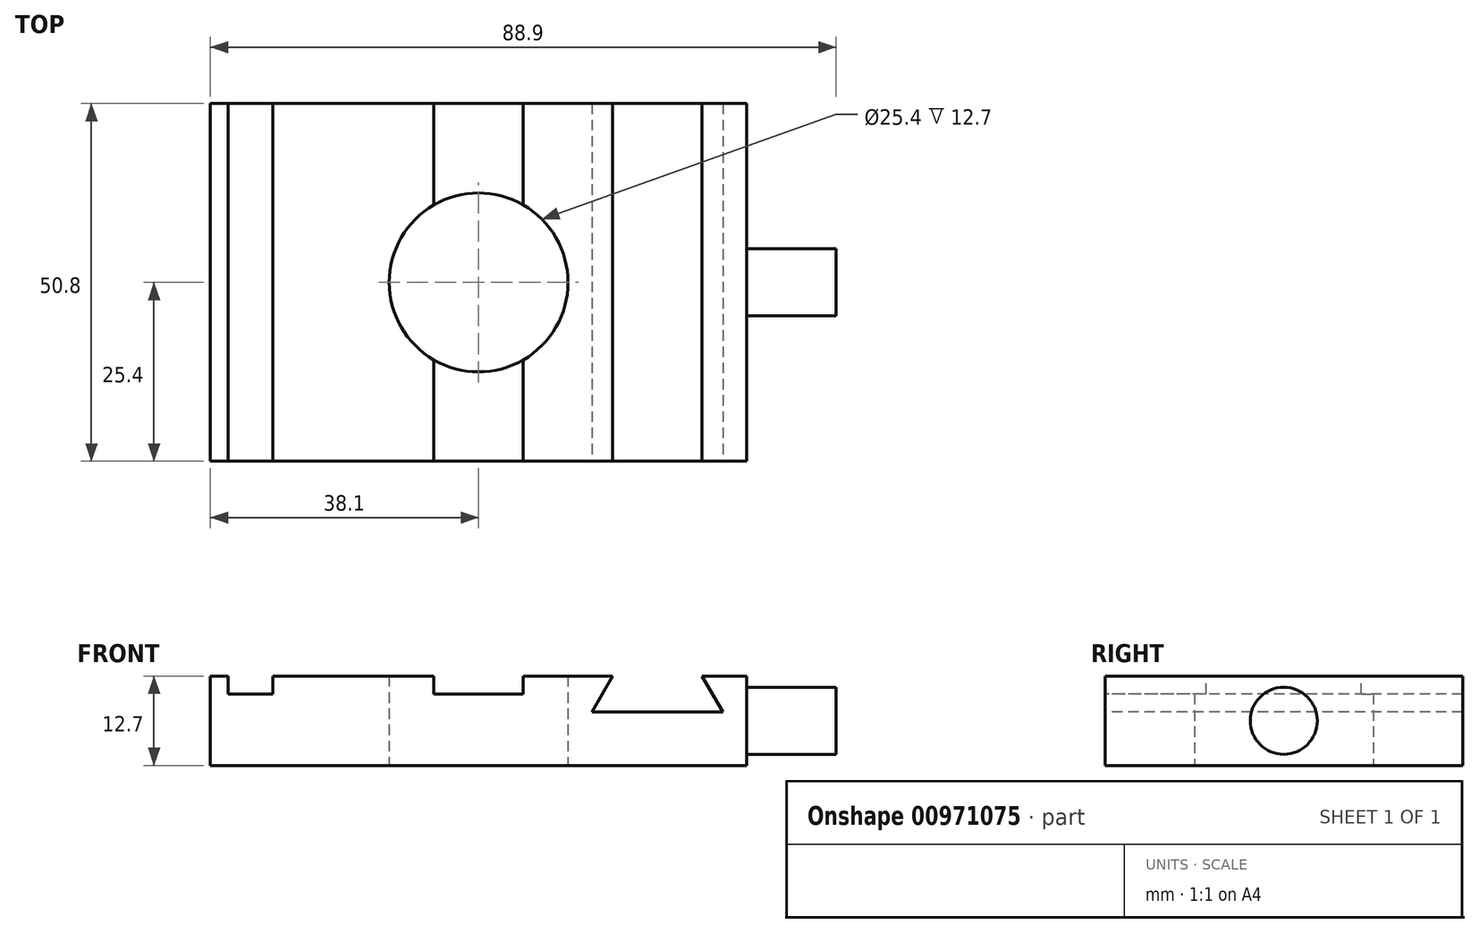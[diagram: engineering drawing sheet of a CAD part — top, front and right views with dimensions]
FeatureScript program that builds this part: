
annotation { "Feature Type Name" : "Feature", "Feature Type Description" : "" }
export const myFeature = defineFeature(function(context is Context, id is Id, definition is map)
    precondition{}
    {
        {
            var Q0;
            Q0=qCreatedBy(makeId("Top.planeOp"),FACE);
            var sketch = newSketch(context, id + "F0", { "sketchPlane" : qUnion([Q0])});
            skLineSegment(sketch, "E0.bottom", {"start": v(-38.1, -25.4) * mm, "end": v(38.1, -25.4) * mm});
            skLineSegment(sketch, "E0.top", {"start": v(-38.1, 25.4) * mm, "end": v(38.1, 25.4) * mm});
            skLineSegment(sketch, "E0.left", {"start": v(-38.1, -25.4) * mm, "end": v(-38.1, 25.4) * mm});
            skLineSegment(sketch, "E0.right", {"start": v(38.1, -25.4) * mm, "end": v(38.1, 25.4) * mm});
            skPoint(sketch, "E0.middle", {"position": v(0, 0) * mm});
            skCircle(sketch, "E1", {"center": v(0, 0) * mm, "radius": 12.7 * mm});
            skSolve(sketch);
        }
        {
            var Q0;
            Q0=makeQuery(id+"F0.imprint","IMPRINT",FACE,{"disambiguationData":[TD([[makeQuery(id+"F0.imprint","IMPRINT",EDGE,{"derivedFrom":sQuery(id+"F0.wireOp",EDGE,"E0.bottom")}),1.0]])]});
            extrude(context, id + "F1", {"entities" : qUnion([Q0]), "depth" : 12.7 * mm, "offsetDistance" : 25.4 * mm});
        }
        {
            var Q0;
            Q0=makeQuery(id+"F1.opExtrude","CAP_FACE",FACE,{"disambiguationData":[OSD([sQuery(id+"F0.wireOp",EDGE,"E0.bottom"),sQuery(id+"F0.wireOp",EDGE,"E0.top"),sQuery(id+"F0.wireOp",EDGE,"E0.left"),sQuery(id+"F0.wireOp",EDGE,"E0.right"),sQuery(id+"F0.wireOp",EDGE,"E1")])],"isStart":false});
            var sketch = newSketch(context, id + "F2", { "sketchPlane" : qUnion([Q0])});
            skLineSegment(sketch, "E2.bottom", {"start": v(-35.56, 25.4) * mm, "end": v(-29.21, 25.4) * mm});
            skLineSegment(sketch, "E2.top", {"start": v(-35.56, -25.4) * mm, "end": v(-29.21, -25.4) * mm});
            skLineSegment(sketch, "E2.left", {"start": v(-35.56, 25.4) * mm, "end": v(-35.56, -25.4) * mm});
            skLineSegment(sketch, "E2.right", {"start": v(-29.21, 25.4) * mm, "end": v(-29.21, -25.4) * mm});
            skLineSegment(sketch, "E3", {"start": v(-6.35, 25.4) * mm, "end": v(-6.35, -25.4) * mm});
            skLineSegment(sketch, "E4", {"start": v(-6.35, -25.4) * mm, "end": v(6.35, -25.4) * mm});
            skLineSegment(sketch, "E5", {"start": v(6.35, -25.4) * mm, "end": v(6.35, 25.4) * mm});
            skLineSegment(sketch, "E6", {"start": v(6.35, 25.4) * mm, "end": v(-6.35, 25.4) * mm});
            skPoint(sketch, "E7", {"position": v(0, 0) * mm});
            skLineSegment(sketch, "E8", {"start": v(0, 25.4) * mm, "end": v(0, -25.4) * mm, "construction": true});
            skSolve(sketch);
        }
        {
            var Q0;
            Q0=makeQuery(id+"F2.imprint","IMPRINT",FACE,{"disambiguationData":[TD([[makeQuery(id+"F2.imprint","IMPRINT",EDGE,{"derivedFrom":sQuery(id+"F2.wireOp",EDGE,"E2.bottom")}),-1.0]])]});
            var Q1;
            {var subQ0=sQuery(id+"F2.wireOp",EDGE,"E4");Q1=makeQuery(id+"F2.imprint","IMPRINT",FACE,{"disambiguationData":[TD([[makeQuery(id+"F2.imprint","IMPRINT",EDGE,{"derivedFrom":subQ0}),1.0]])]});}
            var Q2;
            {var subQ0=sQuery(id+"F2.wireOp",EDGE,"E6");Q2=makeQuery(id+"F2.imprint","IMPRINT",FACE,{"disambiguationData":[TD([[makeQuery(id+"F2.imprint","IMPRINT",EDGE,{"derivedFrom":subQ0}),-1.0]])]});}
            extrude(context, id + "F3", {"entities" : qUnion([Q0, Q1, Q2]), "operationType" : NewBodyOperationType.REMOVE, "oppositeDirection" : true, "depth" : 2.54 * mm, "offsetDistance" : 25.4 * mm});
        }
        {
            var Q0;
            Q0=makeQuery(id+"F1.opExtrude","SWEPT_FACE",FACE,{"disambiguationData":[OSD([sQuery(id+"F0.wireOp",EDGE,"E0.bottom")])]});
            var sketch = newSketch(context, id + "F4", { "sketchPlane" : qUnion([Q0])});
            skLineSegment(sketch, "E9", {"start": v(19.05, 12.7) * mm, "end": v(16.12, 7.62) * mm});
            skLineSegment(sketch, "E10", {"start": v(16.12, 7.62) * mm, "end": v(34.68, 7.62) * mm});
            skLineSegment(sketch, "E11", {"start": v(34.68, 7.62) * mm, "end": v(31.75, 12.7) * mm});
            skLineSegment(sketch, "E12", {"start": v(25.4, 7.62) * mm, "end": v(25.4, 12.7) * mm, "construction": true});
            skSolve(sketch);
        }
        {
            var Q0;
            {var subQ0=sQuery(id+"F4.wireOp",EDGE,"E9");Q0=makeQuery(id+"F4.imprint","IMPRINT",FACE,{"disambiguationData":[TD([[makeQuery(id+"F4.imprint","IMPRINT",EDGE,{"derivedFrom":subQ0}),1.0]])]});}
            extrude(context, id + "F5", {"entities" : qUnion([Q0]), "operationType" : NewBodyOperationType.REMOVE, "endBound" : BoundingType.THROUGH_ALL, "oppositeDirection" : true, "depth" : 25.4 * mm, "offsetDistance" : 25.4 * mm});
        }
        {
            var Q0;
            Q0=makeQuery(id+"F1.opExtrude","SWEPT_FACE",FACE,{"disambiguationData":[OSD([sQuery(id+"F0.wireOp",EDGE,"E0.right")])]});
            var sketch = newSketch(context, id + "F6", { "sketchPlane" : qUnion([Q0])});
            skCircle(sketch, "E13", {"center": v(0, 6.35) * mm, "radius": 4.76 * mm});
            skPoint(sketch, "E13.centerSnap0", {"position": v(-25.4, 6.35) * mm});
            skSolve(sketch);
        }
        {
            var Q0;
            Q0=makeQuery(id+"F6.imprint","IMPRINT",FACE,{"disambiguationData":[TD([[makeQuery(id+"F6.imprint","IMPRINT",EDGE,{"derivedFrom":sQuery(id+"F6.wireOp",EDGE,"E13")}),1.0]])]});
            extrude(context, id + "F7", {"entities" : qUnion([Q0]), "operationType" : NewBodyOperationType.ADD, "depth" : 12.7 * mm, "offsetDistance" : 25.4 * mm});
        }
    });
